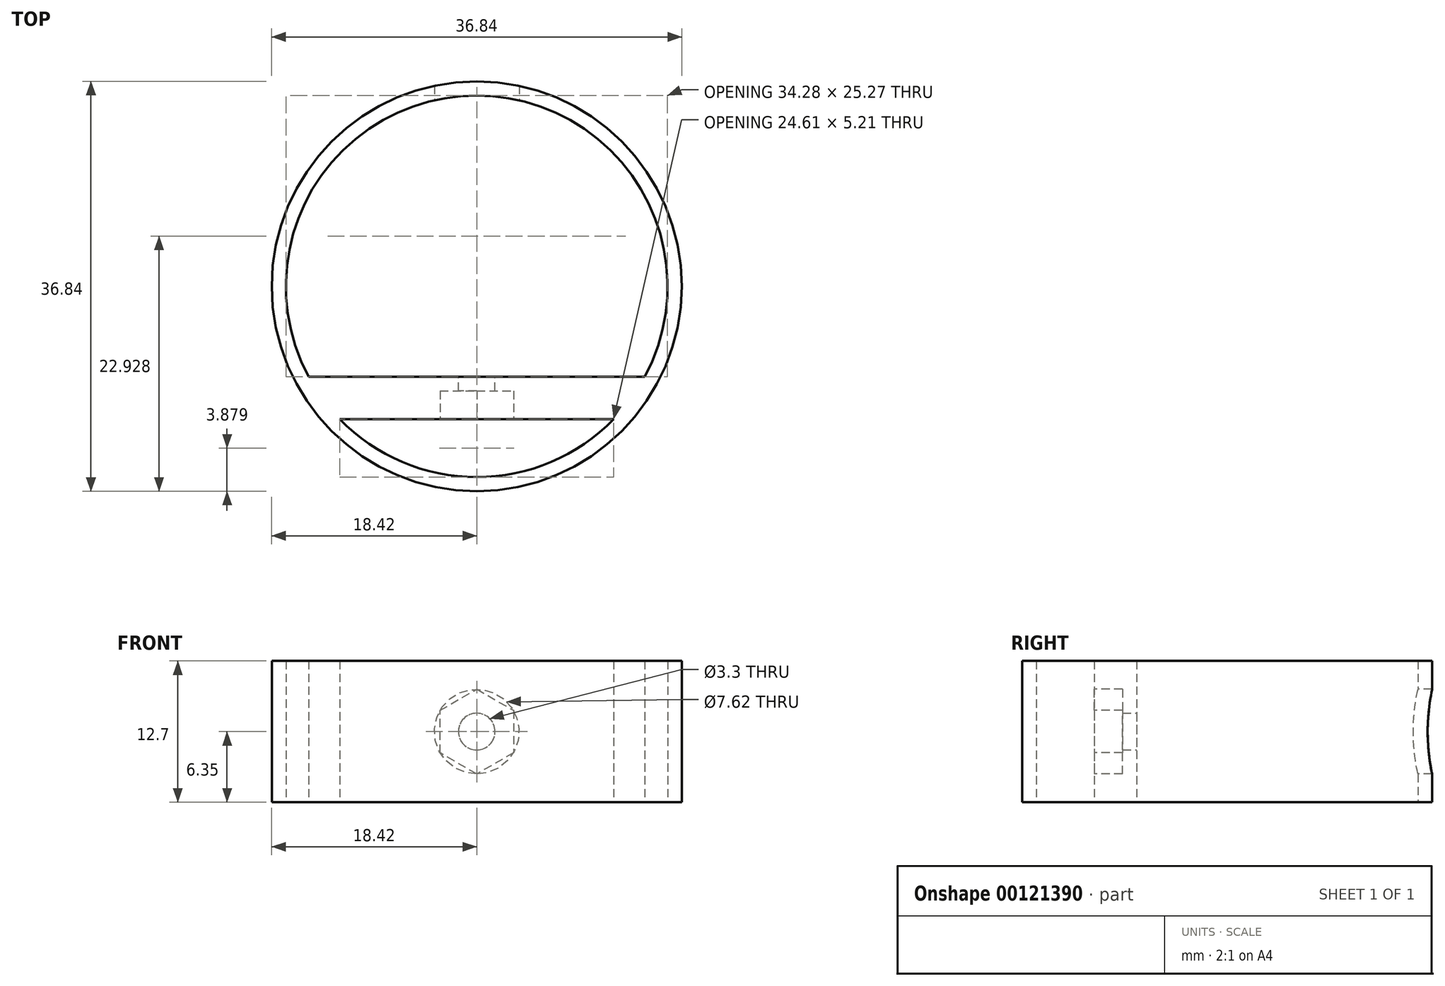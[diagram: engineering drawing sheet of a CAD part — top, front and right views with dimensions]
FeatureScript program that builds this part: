
annotation { "Feature Type Name" : "Feature", "Feature Type Description" : "" }
export const myFeature = defineFeature(function(context is Context, id is Id, definition is map)
    precondition{}
    {
        {
            var Q0;
            Q0=qCreatedBy(makeId("Top.planeOp"),FACE);
            var sketch = newSketch(context, id + "F0", { "sketchPlane" : qUnion([Q0])});
            skCircle(sketch, "E0", {"center": v(0, 0) * mm, "radius": 18.41 * mm});
            skLineSegment(sketch, "E1", {"start": v(-15.1, -8.13) * mm, "end": v(15.1, -8.13) * mm});
            skLineSegment(sketch, "E2", {"start": v(-12.3, -11.94) * mm, "end": v(12.3, -11.94) * mm});
            skArc(sketch, "E3", {"start": v(-15.1, -8.13) * mm, "mid": v(-13.83, -10.13) * mm, "end": v(-12.3, -11.94) * mm, "construction": true});
            skArc(sketch, "E4", {"start": v(-12.3, -11.94) * mm, "mid": v(0, -17.14) * mm, "end": v(12.3, -11.94) * mm});
            skArc(sketch, "E5", {"start": v(15.1, -8.13) * mm, "mid": v(0, 17.14) * mm, "end": v(-15.1, -8.13) * mm});
            skArc(sketch, "E6", {"start": v(12.3, -11.94) * mm, "mid": v(13.83, -10.13) * mm, "end": v(15.1, -8.13) * mm, "construction": true});
            skLineSegment(sketch, "E7", {"start": v(-15.1, -8.13) * mm, "end": v(-16.21, -8.73) * mm, "construction": true});
            skSolve(sketch);
        }
        {
            var Q0;
            Q0=qSketchRegion(id+"F0",true);
            extrude(context, id + "F1", {"entities" : qUnion([Q0]), "depth" : 12.7 * mm});
        }
        {
            var Q0;
            Q0=makeQuery(id+"F1.opExtrude","SWEPT_FACE",FACE,{"disambiguationData":[OSD([sQuery(id+"F0.wireOp",EDGE,"E1")])]});
            var sketch = newSketch(context, id + "F2", { "sketchPlane" : qUnion([Q0])});
            skPoint(sketch, "E8", {"position": v(0, 0) * mm});
            skPoint(sketch, "E9", {"position": v(-15.1, 6.35) * mm});
            skCircle(sketch, "E10", {"center": v(0, 6.35) * mm, "radius": 1.65 * mm});
            skSolve(sketch);
        }
        {
            var Q0;
            Q0=qSketchRegion(id+"F2",true);
            var Q1;
            Q1=makeQuery(id+"F1.opExtrude","SWEPT_FACE",FACE,{"disambiguationData":[OSD([sQuery(id+"F0.wireOp",EDGE,"E2")])]});
            extrude(context, id + "F3", {"entities" : qUnion([Q0]), "operationType" : NewBodyOperationType.REMOVE, "endBound" : BoundingType.UP_TO_SURFACE, "oppositeDirection" : true, "endBoundEntityFace" : qUnion([Q1]), "depth" : 25.4 * mm});
        }
        {
            var Q0;
            Q0=makeQuery(id+"F1.opExtrude","SWEPT_FACE",FACE,{"disambiguationData":[OSD([sQuery(id+"F0.wireOp",EDGE,"E2")])]});
            var sketch = newSketch(context, id + "F4", { "sketchPlane" : qUnion([Q0])});
            skCircle(sketch, "E11.cCircle", {"center": v(0, 6.35) * mm, "radius": 3.3 * mm, "construction": true});
            skLineSegment(sketch, "E11.0", {"start": v(3.3, 8.26) * mm, "end": v(3.3, 4.44) * mm});
            skLineSegment(sketch, "E11.1", {"start": v(3.3, 4.44) * mm, "end": v(0, 2.54) * mm});
            skLineSegment(sketch, "E11.2", {"start": v(0, 2.54) * mm, "end": v(-3.3, 4.44) * mm});
            skLineSegment(sketch, "E11.3", {"start": v(-3.3, 4.44) * mm, "end": v(-3.3, 8.26) * mm});
            skLineSegment(sketch, "E11.4", {"start": v(-3.3, 8.26) * mm, "end": v(0, 10.16) * mm});
            skLineSegment(sketch, "E11.5", {"start": v(0, 10.16) * mm, "end": v(3.3, 8.26) * mm});
            skPoint(sketch, "E11.0.midPoint", {"position": v(3.3, 6.35) * mm});
            skSolve(sketch);
        }
        {
            var Q0;
            Q0=qSketchRegion(id+"F4",true);
            extrude(context, id + "F5", {"entities" : qUnion([Q0]), "operationType" : NewBodyOperationType.REMOVE, "oppositeDirection" : true, "depth" : 2.54 * mm});
        }
        {
            var Q0;
            Q0=makeQuery(id+"F1.opExtrude","SWEPT_FACE",FACE,{"disambiguationData":[OSD([sQuery(id+"F0.wireOp",EDGE,"E1")])]});
            var sketch = newSketch(context, id + "F6", { "sketchPlane" : qUnion([Q0])});
            skCircle(sketch, "E12", {"center": v(0, 6.35) * mm, "radius": 3.81 * mm});
            skSolve(sketch);
        }
        {
            var Q0;
            Q0=qSketchRegion(id+"F6",true);
            extrude(context, id + "F7", {"entities" : qUnion([Q0]), "operationType" : NewBodyOperationType.REMOVE, "endBound" : BoundingType.THROUGH_ALL, "depth" : 25.4 * mm});
        }
    });
